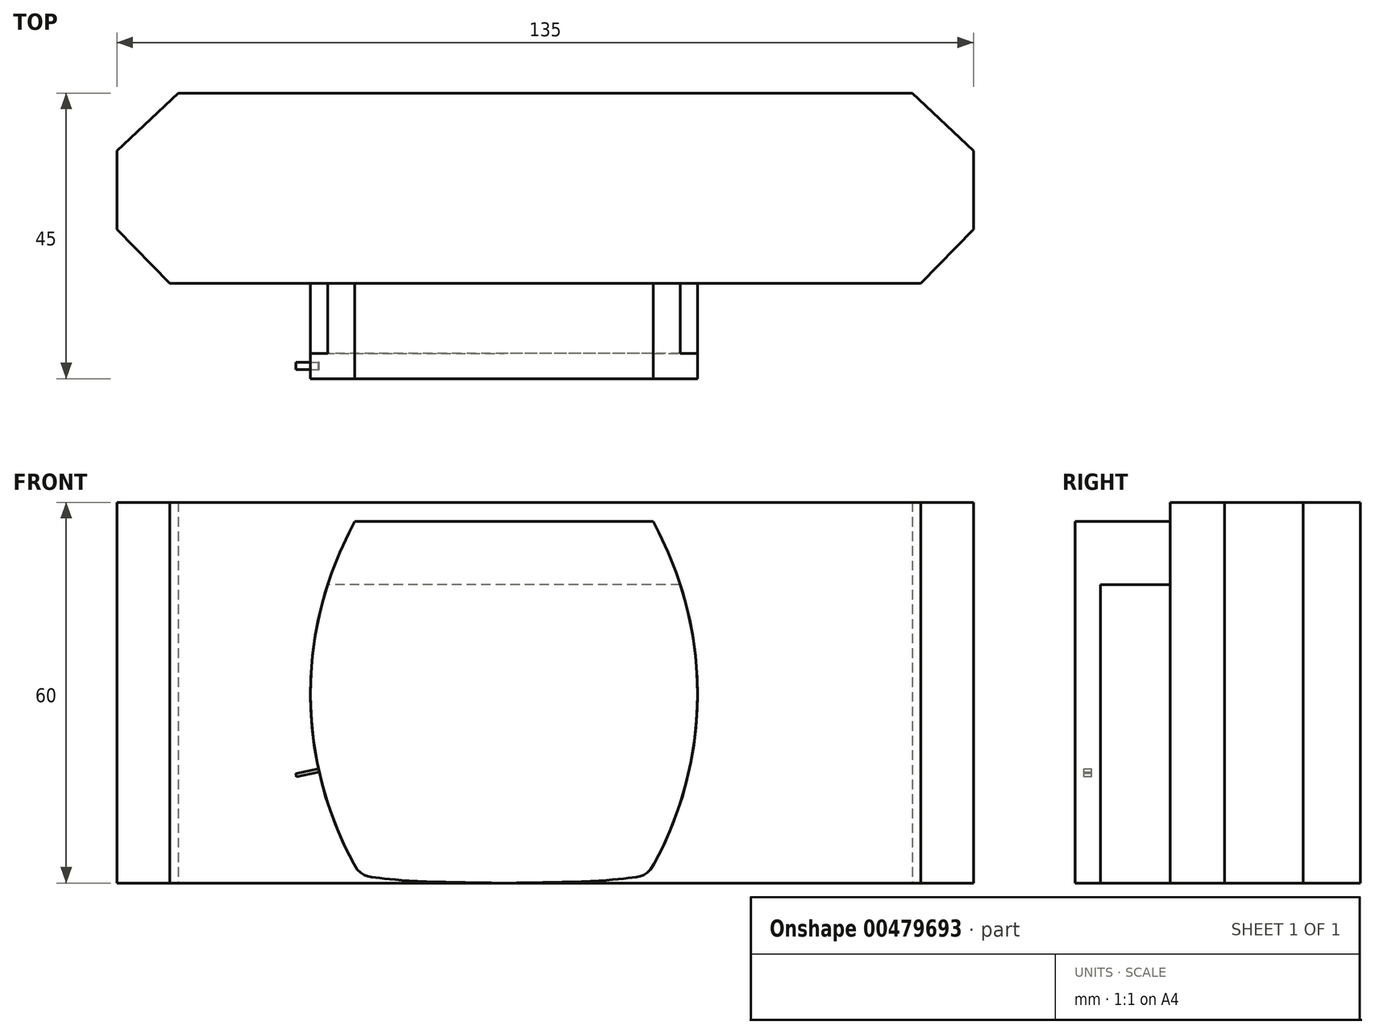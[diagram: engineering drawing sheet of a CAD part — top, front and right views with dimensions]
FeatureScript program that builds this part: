
annotation { "Feature Type Name" : "Feature", "Feature Type Description" : "" }
export const myFeature = defineFeature(function(context is Context, id is Id, definition is map)
    precondition{}
    {
        {
            var Q0;
            Q0=qCreatedBy(makeId("Top.planeOp"),FACE);
            var sketch = newSketch(context, id + "F0", { "sketchPlane" : qUnion([Q0])});
            skLineSegment(sketch, "E0", {"start": v(-52.67, 0) * mm, "end": v(65.67, 0) * mm});
            skLineSegment(sketch, "E1", {"start": v(0, 95.26) * mm, "end": v(0, -60.64) * mm, "construction": true});
            skLineSegment(sketch, "E2", {"start": v(-51.34, 30) * mm, "end": v(64.34, 30) * mm});
            skLineSegment(sketch, "E3", {"start": v(64.34, 30) * mm, "end": v(74, 20.92) * mm});
            skLineSegment(sketch, "E4", {"start": v(74, 20.92) * mm, "end": v(74, 8.54) * mm});
            skLineSegment(sketch, "E5", {"start": v(74, 8.54) * mm, "end": v(65.67, 0) * mm});
            skLineSegment(sketch, "E6", {"start": v(-51.34, 30) * mm, "end": v(-61, 20.92) * mm});
            skLineSegment(sketch, "E7", {"start": v(-61, 20.92) * mm, "end": v(-61, 8.54) * mm});
            skLineSegment(sketch, "E8", {"start": v(-61, 8.54) * mm, "end": v(-52.67, 0) * mm});
            skLineSegment(sketch, "E9", {"start": v(-61, 20.92) * mm, "end": v(74, 20.92) * mm, "construction": true});
            skLineSegment(sketch, "E10", {"start": v(-61, 8.54) * mm, "end": v(74, 8.54) * mm, "construction": true});
            skSolve(sketch);
        }
        {
            var Q0;
            Q0=makeQuery(id+"F0.imprint","IMPRINT",FACE,{"disambiguationData":[TD([[makeQuery(id+"F0.imprint","IMPRINT",EDGE,{"derivedFrom":sQuery(id+"F0.wireOp",EDGE,"E0")}),1.0]])]});
            extrude(context, id + "F1", {"entities" : qUnion([Q0]), "depth" : 60 * mm});
        }
        {
            var Q0;
            Q0=makeQuery(id+"F1.opExtrude","SWEPT_FACE",FACE,{"disambiguationData":[OSD([sQuery(id+"F0.wireOp",EDGE,"E0")])]});
            var sketch = newSketch(context, id + "F2", { "sketchPlane" : qUnion([Q0])});
            skLineSegment(sketch, "E11", {"start": v(0, 60) * mm, "end": v(0, 0) * mm, "construction": true});
            skLineSegment(sketch, "E12", {"start": v(-23.5, 57) * mm, "end": v(0, 57) * mm});
            skLineSegment(sketch, "E13", {"start": v(-23.5, 57) * mm, "end": v(-24.4, 55.22) * mm});
            skArc(sketch, "E14", {"start": v(-24.4, 55.22) * mm, "mid": v(-30.5, 29.02) * mm, "end": v(-23.65, 3) * mm});
            skFitSpline(sketch, "E15", {"points": [v(-23.65, 3) * mm, v(-20.63, 0.93) * mm, v(-14.57, 0.36) * mm, v(0, 0) * mm], "startDerivative": vector(12.52, -22.94) * mm, "endDerivative": vector(17.96, 0) * mm});
            skLineSegment(sketch, "E16", {"start": v(-30.5, 60) * mm, "end": v(-30.5, 0) * mm, "construction": true});
            skLineSegment(sketch, "E17.MirrorCS", {"start": v(23.5, 57) * mm, "end": v(0, 57) * mm});
            skLineSegment(sketch, "E18.MirrorCS", {"start": v(23.5, 57) * mm, "end": v(24.4, 55.22) * mm});
            skArc(sketch, "E19.MirrorCS", {"start": v(24.4, 55.22) * mm, "mid": v(30.5, 29.02) * mm, "end": v(23.65, 3) * mm});
            skFitSpline(sketch, "E20.MirrorCS", {"points": [v(23.65, 3) * mm, v(20.63, 0.93) * mm, v(14.57, 0.36) * mm, v(0, 0) * mm], "startDerivative": vector(-12.52, -22.94) * mm, "endDerivative": vector(-17.96, 0) * mm});
            skSolve(sketch);
        }
        {
            var Q0;
            Q0=makeQuery(id+"F2.imprint","IMPRINT",FACE,{"disambiguationData":[TD([[makeQuery(id+"F2.imprint","IMPRINT",EDGE,{"derivedFrom":sQuery(id+"F2.wireOp",EDGE,"E12")}),-1.0]])]});
            extrude(context, id + "F3", {"entities" : qUnion([Q0]), "depth" : 15 * mm});
        }
        {
            var Q0;
            Q0=makeQuery(id+"F1.opExtrude","SWEPT_FACE",FACE,{"disambiguationData":[OSD([sQuery(id+"F0.wireOp",EDGE,"E0")])]});
            var sketch = newSketch(context, id + "F4", { "sketchPlane" : qUnion([Q0])});
            skLineSegment(sketch, "E21", {"start": v(46.92, 0) * mm, "end": v(46.92, 47) * mm});
            skLineSegment(sketch, "E22", {"start": v(46.92, 47) * mm, "end": v(-40.47, 47) * mm});
            skLineSegment(sketch, "E23", {"start": v(-40.47, 47) * mm, "end": v(-40.47, 0) * mm});
            skLineSegment(sketch, "E24", {"start": v(-40.47, 0) * mm, "end": v(46.92, 0) * mm});
            skSolve(sketch);
        }
        {
            var Q0;
            Q0 = qSketchRegion(id + "F4", true);
            extrude(context, id + "F5", {"entities" : qUnion([Q0]), "operationType" : NewBodyOperationType.REMOVE, "depth" : 11 * mm});
        }
        {
            var Q0;
            Q0=makeQuery(id+"F5.boolean.opBoolean","COPY",FACE,{"derivedFrom":makeQuery(id+"F5.opExtrude","CAP_FACE",FACE,{"disambiguationData":[OSD([sQuery(id+"F4.wireOp",EDGE,"E21"),sQuery(id+"F4.wireOp",EDGE,"E22"),sQuery(id+"F4.wireOp",EDGE,"E23"),sQuery(id+"F4.wireOp",EDGE,"E24")])],"isStart":false})});
            extrude(context, id + "F6", {"entities" : qUnion([Q0]), "depth" : 11 * mm});
        }
        {
            var Q0;
            Q0=makeQuery(id+"F3.opExtrude","CAP_FACE",FACE,{"disambiguationData":[OSD([sQuery(id+"F2.wireOp",EDGE,"E12"),sQuery(id+"F2.wireOp",EDGE,"E13"),sQuery(id+"F2.wireOp",EDGE,"E14"),sQuery(id+"F2.wireOp",EDGE,"E15"),sQuery(id+"F2.wireOp",EDGE,"E17.MirrorCS"),sQuery(id+"F2.wireOp",EDGE,"E18.MirrorCS"),sQuery(id+"F2.wireOp",EDGE,"E19.MirrorCS"),sQuery(id+"F2.wireOp",EDGE,"E20.MirrorCS")])],"isStart":false});
            var sketch = newSketch(context, id + "F7", { "sketchPlane" : qUnion([Q0])});
            skPoint(sketch, "E25", {"position": v(-29.24, 18) * mm});
            skSolve(sketch);
        }
        {
            var Q0;
            Q0=sQuery(id+"F7.wireOp",VERTEX,"E25");
            var Q1;
            Q1=makeQuery(id+"F3.opExtrude","CAP_EDGE",EDGE,{"disambiguationData":[OSD([sQuery(id+"F2.wireOp",EDGE,"E14")])],"isStart":false});
            cPlane(context, id + "F8", {"entities" : qUnion([Q0, Q1]), "cplaneType" : CPlaneType.CURVE_POINT, "offset" : 25 * mm, "width" : 150 * mm, "height" : 150 * mm});
        }
        {
            var Q0;
            Q0=qCreatedBy(id+"F8.planeOp",FACE);
            var sketch = newSketch(context, id + "F9", { "sketchPlane" : qUnion([Q0])});
            skLineSegment(sketch, "E26", {"start": v(-24.78, 15) * mm, "end": v(-24.78, 11) * mm, "construction": true});
            skLineSegment(sketch, "E27", {"start": v(-28.65, 13) * mm, "end": v(-24.78, 13) * mm, "construction": true});
            skPoint(sketch, "E27.startSnap0", {"position": v(-24.78, 13) * mm});
            skLineSegment(sketch, "E28", {"start": v(-28.45, 12.41) * mm, "end": v(-28.45, 13.59) * mm});
            skPoint(sketch, "E29", {"position": v(-28.45, 13) * mm});
            skLineSegment(sketch, "E30", {"start": v(-28.45, 12.41) * mm, "end": v(-24.78, 12.41) * mm});
            skLineSegment(sketch, "E31", {"start": v(-28.45, 13.59) * mm, "end": v(-24.78, 13.59) * mm});
            skLineSegment(sketch, "E32", {"start": v(-24.78, 13.59) * mm, "end": v(-24.78, 12.41) * mm});
            skSolve(sketch);
        }
        {
            var Q0;
            Q0=makeQuery(id+"F9.imprint","IMPRINT",FACE,{"disambiguationData":[TD([[makeQuery(id+"F9.imprint","IMPRINT",EDGE,{"derivedFrom":sQuery(id+"F9.wireOp",EDGE,"E28")}),-1.0]])]});
            extrude(context, id + "F10", {"entities" : qUnion([Q0]), "depth" : .5 * mm});
        }
    });
